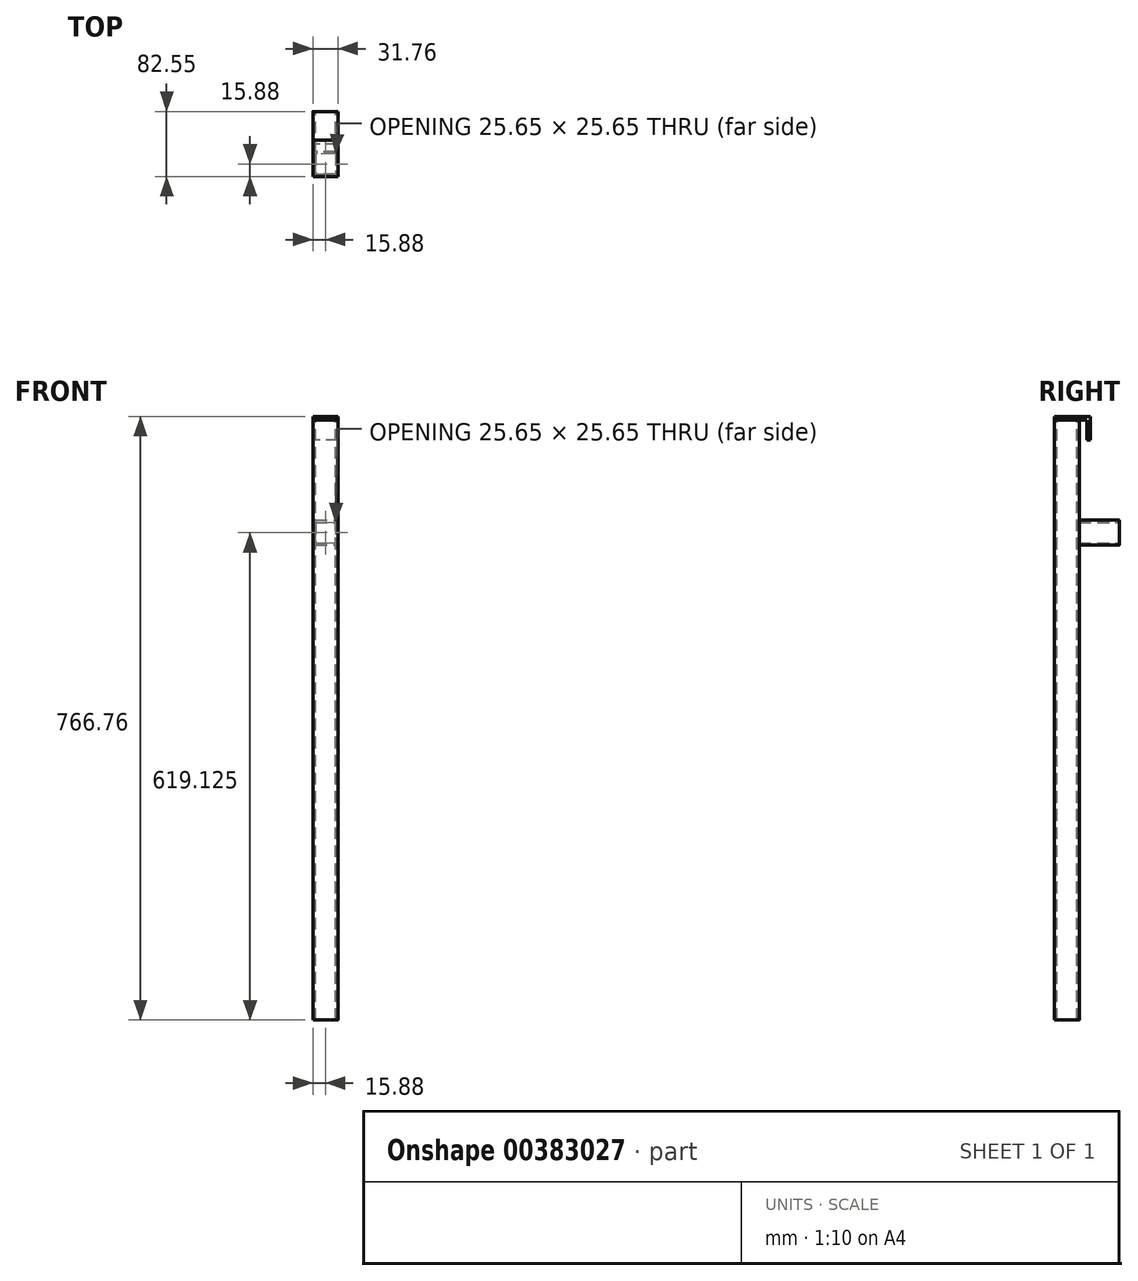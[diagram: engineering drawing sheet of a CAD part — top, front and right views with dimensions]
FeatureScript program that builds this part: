
annotation { "Feature Type Name" : "Feature", "Feature Type Description" : "" }
export const myFeature = defineFeature(function(context is Context, id is Id, definition is map)
    precondition{}
    {
        {
            var Q0;
            Q0=qCreatedBy(makeId("Top.planeOp"),FACE);
            var sketch = newSketch(context, id + "F0", { "sketchPlane" : qUnion([Q0])});
            skLineSegment(sketch, "E0.bottom", {"start": v(15.88, 15.88) * mm, "end": v(-15.88, 15.88) * mm});
            skLineSegment(sketch, "E0.top", {"start": v(15.88, -15.88) * mm, "end": v(-15.88, -15.88) * mm});
            skLineSegment(sketch, "E0.left", {"start": v(15.88, 15.88) * mm, "end": v(15.88, -15.88) * mm});
            skLineSegment(sketch, "E0.right", {"start": v(-15.88, 15.88) * mm, "end": v(-15.88, -15.88) * mm});
            skPoint(sketch, "E0.middle", {"position": v(0, 0) * mm});
            skSolve(sketch);
        }
        {
            var Q0;
            Q0 = qSketchRegion(id + "F0", true);
            extrude(context, id + "F1", {"entities" : qUnion([Q0]), "oppositeDirection" : true, "depth" : 762 * mm});
        }
        {
            var Q0;
            Q0=makeQuery(id+"F1.opExtrude","SWEPT_EDGE",EDGE,{"disambiguationData":[OSD([sQuery(id+"F0.wireOp",EDGE,"E0.bottom"),sQuery(id+"F0.wireOp",EDGE,"E0.right")])]});
            var Q1;
            Q1=makeQuery(id+"F1.opExtrude","SWEPT_EDGE",EDGE,{"disambiguationData":[OSD([sQuery(id+"F0.wireOp",EDGE,"E0.top"),sQuery(id+"F0.wireOp",EDGE,"E0.right")])]});
            var Q2;
            Q2=makeQuery(id+"F1.opExtrude","SWEPT_EDGE",EDGE,{"disambiguationData":[OSD([sQuery(id+"F0.wireOp",EDGE,"E0.bottom"),sQuery(id+"F0.wireOp",EDGE,"E0.left")])]});
            var Q3;
            Q3=makeQuery(id+"F1.opExtrude","SWEPT_EDGE",EDGE,{"disambiguationData":[OSD([sQuery(id+"F0.wireOp",EDGE,"E0.top"),sQuery(id+"F0.wireOp",EDGE,"E0.left")])]});
            fillet(context, id + "F2", {"entities" : qUnion([Q0, Q1, Q2, Q3]), "radius" : 3.17 * mm, "tangentPropagation" : true, "allowEdgeOverflow" : false});
        }
        {
            var Q0;
            Q0=makeQuery(id+"F1.opExtrude","CAP_FACE",FACE,{"disambiguationData":[OSD([sQuery(id+"F0.wireOp",EDGE,"E0.bottom"),sQuery(id+"F0.wireOp",EDGE,"E0.top"),sQuery(id+"F0.wireOp",EDGE,"E0.left"),sQuery(id+"F0.wireOp",EDGE,"E0.right")])],"isStart":true});
            var Q1;
            Q1=makeQuery(id+"F1.opExtrude","CAP_FACE",FACE,{"disambiguationData":[OSD([sQuery(id+"F0.wireOp",EDGE,"E0.bottom"),sQuery(id+"F0.wireOp",EDGE,"E0.top"),sQuery(id+"F0.wireOp",EDGE,"E0.left"),sQuery(id+"F0.wireOp",EDGE,"E0.right")])],"isStart":false});
            shell(context, id + "F3", {"entities" : qUnion([Q0, Q1]), "thickness" : 3.05 * mm});
        }
        {
            var Q0;
            Q0=qCreatedBy(makeId("Right.planeOp"),FACE);
            var sketch = newSketch(context, id + "F4", { "sketchPlane" : qUnion([Q0])});
            skLineSegment(sketch, "E1", {"start": v(-15.88, 4.76) * mm, "end": v(30.16, 4.76) * mm});
            skLineSegment(sketch, "E2", {"start": v(30.16, 4.76) * mm, "end": v(30.16, -25.4) * mm});
            skLineSegment(sketch, "E3", {"start": v(30.16, -25.4) * mm, "end": v(25.4, -25.4) * mm});
            skLineSegment(sketch, "E4", {"start": v(25.4, -25.4) * mm, "end": v(25.4, 0) * mm});
            skLineSegment(sketch, "E5", {"start": v(25.4, 0) * mm, "end": v(-15.88, 0) * mm});
            skLineSegment(sketch, "E6", {"start": v(-15.88, 0) * mm, "end": v(-15.88, 4.76) * mm});
            skSolve(sketch);
        }
        {
            var Q0;
            Q0=makeQuery(id+"F4.imprint","IMPRINT",FACE,{"disambiguationData":[TD([[makeQuery(id+"F4.imprint","IMPRINT",EDGE,{"derivedFrom":sQuery(id+"F4.wireOp",EDGE,"E1")}),-1.0]])]});
            extrude(context, id + "F5", {"entities" : qUnion([Q0]), "endBound" : BoundingType.SYMMETRIC, "depth" : 31.75 * mm});
        }
        {
            var Q0;
            Q0=makeQuery(id+"F1.opExtrude","SWEPT_FACE",FACE,{"disambiguationData":[OSD([sQuery(id+"F0.wireOp",EDGE,"E0.bottom")])]});
            var sketch = newSketch(context, id + "F6", { "sketchPlane" : qUnion([Q0])});
            skLineSegment(sketch, "E7.bottom", {"start": v(15.87, -127) * mm, "end": v(-15.88, -127) * mm});
            skLineSegment(sketch, "E7.top", {"start": v(15.87, -158.75) * mm, "end": v(-15.88, -158.75) * mm});
            skLineSegment(sketch, "E7.left", {"start": v(15.87, -127) * mm, "end": v(15.87, -158.75) * mm});
            skLineSegment(sketch, "E7.right", {"start": v(-15.88, -127) * mm, "end": v(-15.88, -158.75) * mm});
            skPoint(sketch, "E7.middle", {"position": v(0, -142.88) * mm});
            skSolve(sketch);
        }
        {
            var Q0;
            Q0 = qSketchRegion(id + "F6", true);
            extrude(context, id + "F7", {"entities" : qUnion([Q0]), "depth" : 50.8 * mm});
        }
        {
            var Q0;
            Q0=makeQuery(id+"F7.opExtrude","SWEPT_EDGE",EDGE,{"disambiguationData":[OSD([sQuery(id+"F6.wireOp",EDGE,"E7.bottom"),sQuery(id+"F6.wireOp",EDGE,"E7.left")])]});
            var Q1;
            Q1=makeQuery(id+"F7.opExtrude","SWEPT_EDGE",EDGE,{"disambiguationData":[OSD([sQuery(id+"F6.wireOp",EDGE,"E7.top"),sQuery(id+"F6.wireOp",EDGE,"E7.left")])]});
            var Q2;
            Q2=makeQuery(id+"F7.opExtrude","SWEPT_EDGE",EDGE,{"disambiguationData":[OSD([sQuery(id+"F6.wireOp",EDGE,"E7.bottom"),sQuery(id+"F6.wireOp",EDGE,"E7.right")])]});
            var Q3;
            Q3=makeQuery(id+"F7.opExtrude","SWEPT_EDGE",EDGE,{"disambiguationData":[OSD([sQuery(id+"F6.wireOp",EDGE,"E7.top"),sQuery(id+"F6.wireOp",EDGE,"E7.right")])]});
            fillet(context, id + "F8", {"entities" : qUnion([Q0, Q1, Q2, Q3]), "radius" : 3.17 * mm, "tangentPropagation" : true, "allowEdgeOverflow" : false});
        }
        {
            var Q0;
            Q0=makeQuery(id+"F7.opExtrude","CAP_FACE",FACE,{"disambiguationData":[OSD([sQuery(id+"F6.wireOp",EDGE,"E7.bottom"),sQuery(id+"F6.wireOp",EDGE,"E7.top"),sQuery(id+"F6.wireOp",EDGE,"E7.left"),sQuery(id+"F6.wireOp",EDGE,"E7.right")])],"isStart":false});
            var Q1;
            Q1=makeQuery(id+"F7.opExtrude","CAP_FACE",FACE,{"disambiguationData":[OSD([sQuery(id+"F6.wireOp",EDGE,"E7.bottom"),sQuery(id+"F6.wireOp",EDGE,"E7.top"),sQuery(id+"F6.wireOp",EDGE,"E7.left"),sQuery(id+"F6.wireOp",EDGE,"E7.right")])],"isStart":true});
            shell(context, id + "F9", {"entities" : qUnion([Q0, Q1]), "thickness" : 3.05 * mm});
        }
    });
